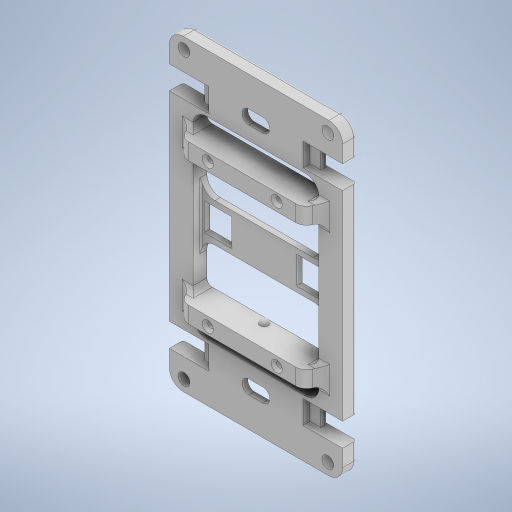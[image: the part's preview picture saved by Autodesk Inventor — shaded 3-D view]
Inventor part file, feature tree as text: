
AUTODESK INVENTOR PART (.ipt)
format: ipt  version: 2023 (Build 270158000, 158)  size: 603,136 bytes
history: native  units: mm
features: extrude x11, sketch x10, fillet x9, other x3, mirror x3, chamfer x1, revolve x1, projected_geometry x1
ambient origin geometry x8: Origin, YZ Plane, XZ Plane, XY Plane, X Axis, Y Axis, Z Axis, Center Point
bodies: Body1 (feature_tree)
feature tree (39):
  other  "솔리드1"
  extrude  "돌출1"  Depth=63.1mm
  extrude  "돌출2"  Depth=112.2mm
  extrude  "돌출3"  Depth=45.85mm
  fillet  "모깎기1"  Radius=70.23mm
  sketch  "스케치4"
  extrude  "돌출4"  Depth=5.0mm TaperAngle=0.0deg
  extrude  "돌출5"  Depth=5.0mm
  mirror  "미러1"
  mirror  "미러2"
  extrude  "돌출6"  Depth=5.0mm
  fillet  "모깎기2"  Radius=5.0mm
  mirror  "미러3"
  fillet  "모깎기3"  Radius=10.0mm
  extrude  "돌출7"  Depth=104.0mm
  fillet  "모깎기4"  Radius=4.2mm
  fillet  "모깎기5"  Radius=52.4mm
  other  "작업 평면1"
  sketch  "스케치9"
  extrude  "돌출8"  TaperAngle=0.0deg  [1 undecoded]
  extrude  "돌출9"  Depth=5.0mm
  fillet  "모깎기7"  Radius=7.0mm
  fillet  "모깎기8"  Radius=8.5mm
  chamfer  "모따기1"  Distance=3.4mm
  other  "작업 평면2"
  revolve  "회전1"
  extrude  "돌출10"  Depth=11.2mm
  fillet  "모깎기9"  Radius=4.0mm
  fillet  "모깎기10"  [1 undecoded]
  extrude  "돌출11"  Depth=2.5mm TaperAngle=0.0deg
  sketch  "스케치1"
  sketch  "스케치2"
  sketch  "스케치3"
  sketch  "스케치6"
  projected_geometry  "투영된 루프1"
  sketch  "스케치8"
  sketch  "스케치11"
  sketch  "스케치13"
  sketch  "스케치14"
note: 2 required parameter values undecoded (feature->parameter linkage not recoverable at this tier; creation-order binding heuristic only, values carry confidence <= 0.55)
